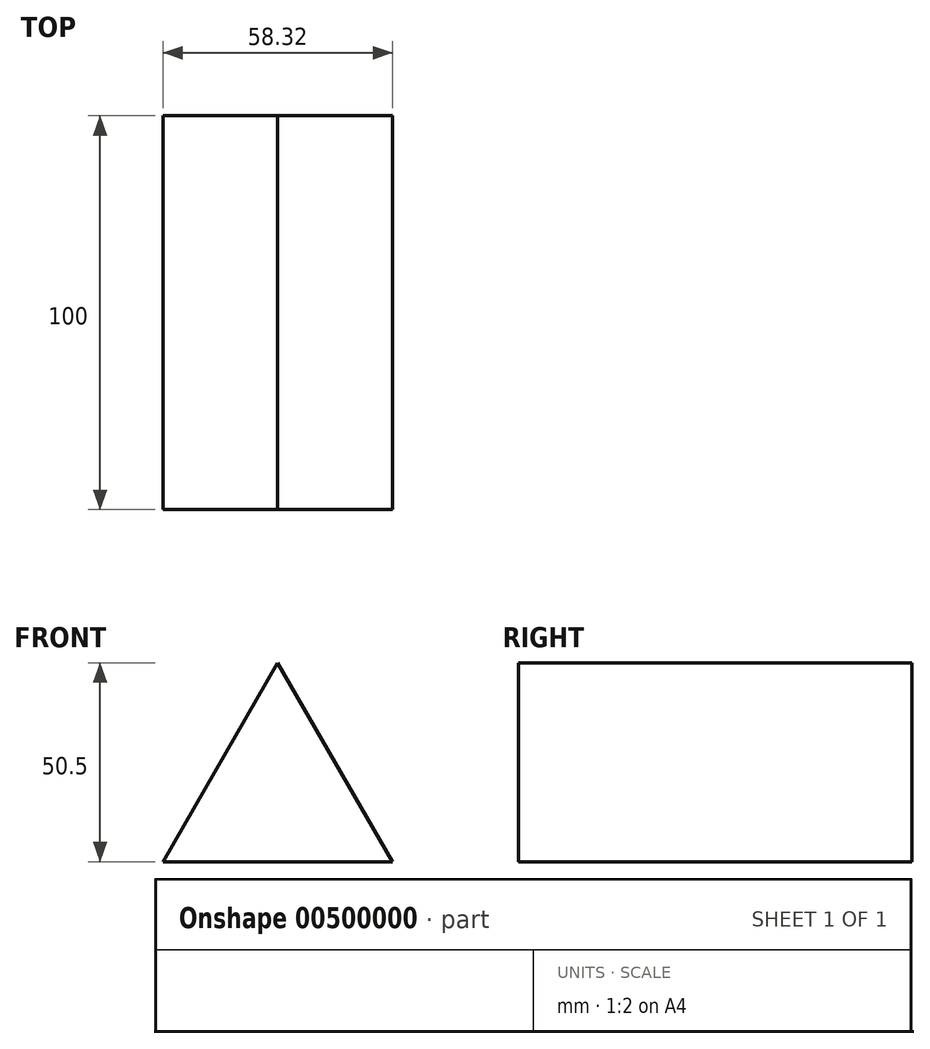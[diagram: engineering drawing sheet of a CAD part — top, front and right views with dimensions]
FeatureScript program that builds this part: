
annotation { "Feature Type Name" : "Feature", "Feature Type Description" : "" }
export const myFeature = defineFeature(function(context is Context, id is Id, definition is map)
    precondition{}
    {
        {
            var Q0;
            Q0=qCreatedBy(makeId("Front.planeOp"),FACE);
            var sketch = newSketch(context, id + "F0", { "sketchPlane" : qUnion([Q0])});
            skCircle(sketch, "E0.cCircle", {"center": v(0, 0) * mm, "radius": 33.67 * mm, "construction": true});
            skLineSegment(sketch, "E0.0", {"start": v(0, 33.67) * mm, "end": v(29.16, -16.83) * mm});
            skLineSegment(sketch, "E0.1", {"start": v(29.16, -16.83) * mm, "end": v(-29.16, -16.83) * mm});
            skLineSegment(sketch, "E0.2", {"start": v(-29.16, -16.83) * mm, "end": v(0, 33.67) * mm});
            skSolve(sketch);
        }
        {
            var Q0;
            Q0 = qSketchRegion(id + "F0", true);
            extrude(context, id + "F1", {"entities" : qUnion([Q0]), "endBound" : BoundingType.SYMMETRIC, "depth" : 100 * mm});
        }
    });
